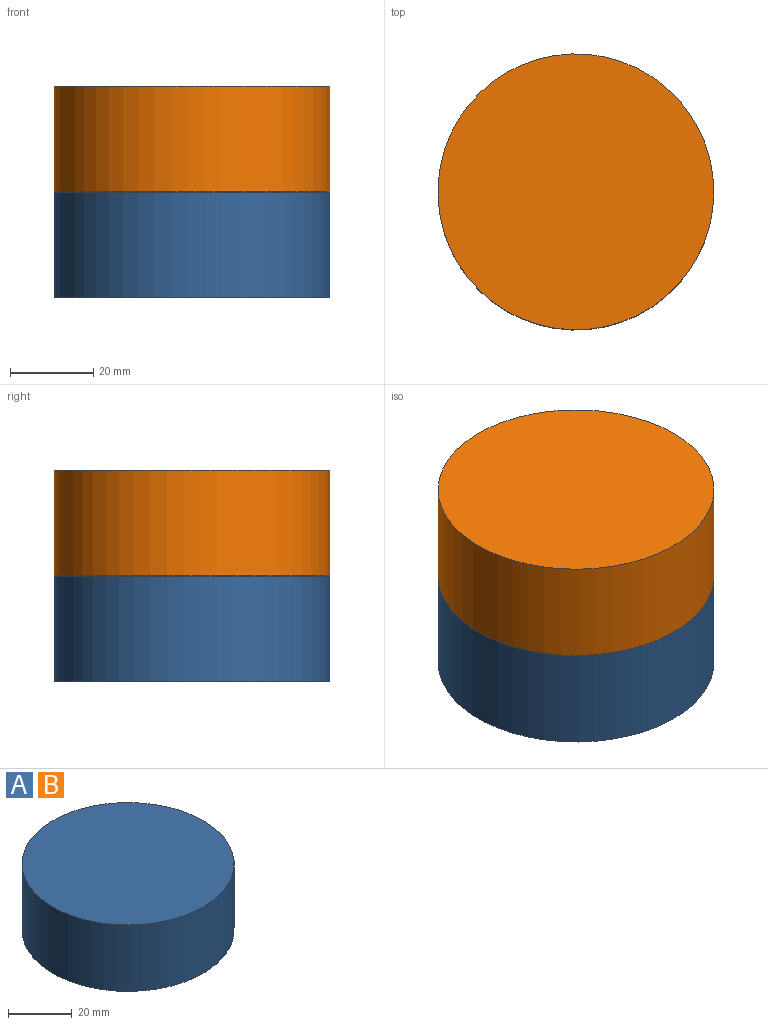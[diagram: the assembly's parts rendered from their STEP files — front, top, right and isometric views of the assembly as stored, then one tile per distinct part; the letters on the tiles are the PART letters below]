
ASSEMBLY  parts=2 mates=1
PART A: 3 faces, bbox 66.3x66.3x25.4 mm
  f0: cylinder r=33.16mm len=66.31mm, axis (0,0,-1), area 5291.5mm2, adj f1,f2
  f1: plane 66.31x66.31mm, normal (0,0,1), area 3453.6mm2, adj f0
  f2: plane 66.31x66.31mm, normal (0,0,-1), area 3453.6mm2, adj f0
PART B: same geometry as A
PLACE A t=(55.08,12.39,0)mm
PLACE B t=(55.08,12.39,25.46)mm
MATE cylindrical B.f0 <-> A.f0  axis (0,0,-1) through (55.08,12.39,38.16)mm
